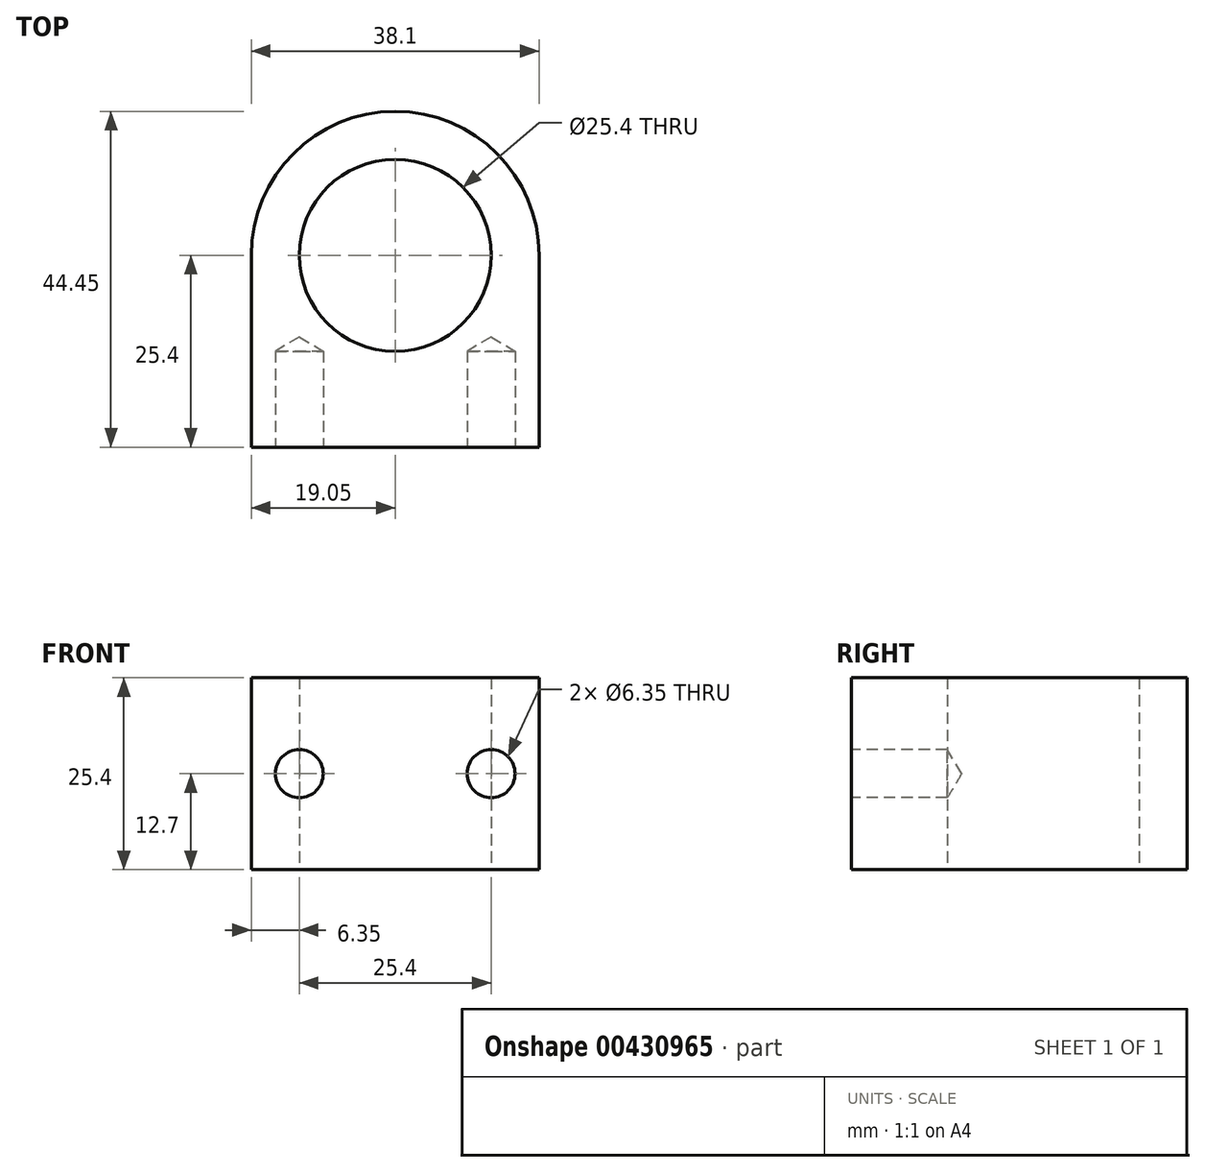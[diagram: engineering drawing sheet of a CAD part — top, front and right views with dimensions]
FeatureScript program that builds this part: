
annotation { "Feature Type Name" : "Feature", "Feature Type Description" : "" }
export const myFeature = defineFeature(function(context is Context, id is Id, definition is map)
    precondition{}
    {
        {
            var Q0;
            Q0=qCreatedBy(makeId("Top.planeOp"),FACE);
            var sketch = newSketch(context, id + "F0", { "sketchPlane" : qUnion([Q0])});
            skLineSegment(sketch, "E0", {"start": v(-19.05, 0) * mm, "end": v(-19.05, -25.4) * mm});
            skLineSegment(sketch, "E1", {"start": v(-19.05, -25.4) * mm, "end": v(19.05, -25.4) * mm});
            skLineSegment(sketch, "E2", {"start": v(19.05, -25.4) * mm, "end": v(19.05, 0) * mm});
            skArc(sketch, "E3", {"start": v(19.05, 0) * mm, "mid": v(0, 19.05) * mm, "end": v(-19.05, 0) * mm});
            skCircle(sketch, "E4", {"center": v(0, 0) * mm, "radius": 12.7 * mm});
            skSolve(sketch);
        }
        {
            var Q0;
            Q0 = qSketchRegion(id + "F0", true);
            extrude(context, id + "F1", {"entities" : qUnion([Q0]), "endBound" : BoundingType.SYMMETRIC, "depth" : 25.4 * mm});
        }
        {
            var Q0;
            Q0=makeQuery(id+"F1.opExtrude","SWEPT_FACE",FACE,{"disambiguationData":[OSD([sQuery(id+"F0.wireOp",EDGE,"E1")])]});
            var sketch = newSketch(context, id + "F2", { "sketchPlane" : qUnion([Q0])});
            skPoint(sketch, "E5", {"position": v(-12.7, 0) * mm});
            skPoint(sketch, "E6", {"position": v(12.7, 0) * mm});
            skSolve(sketch);
        }
        {
            var Q0;
            Q0=sQuery(id+"F2.wireOp",VERTEX,"E5");
            var Q1;
            Q1=sQuery(id+"F2.wireOp",VERTEX,"E6");
            var Q2;
            Q2=makeQuery(id+"F1.opExtrude","SWEPT_BODY",BODY,{"disambiguationData":[OSD([sQuery(id+"F0.wireOp",EDGE,"E0"),sQuery(id+"F0.wireOp",EDGE,"E1"),sQuery(id+"F0.wireOp",EDGE,"E2"),sQuery(id+"F0.wireOp",EDGE,"E3"),sQuery(id+"F0.wireOp",EDGE,"E4")])]});
            hole(context, id + "F3", {"style" : HoleStyle.SIMPLE, "endStyle" : HoleEndStyle.BLIND, "holeDiameter" : 6.35 * mm, "holeDepth" : 12.7 * mm, "isTappedThrough" : true, "tappedDepth" : 12.7 * mm, "tapClearance" : 3, "locations" : qUnion([Q0, Q1]), "scope" : qUnion([Q2])});
        }
    });
